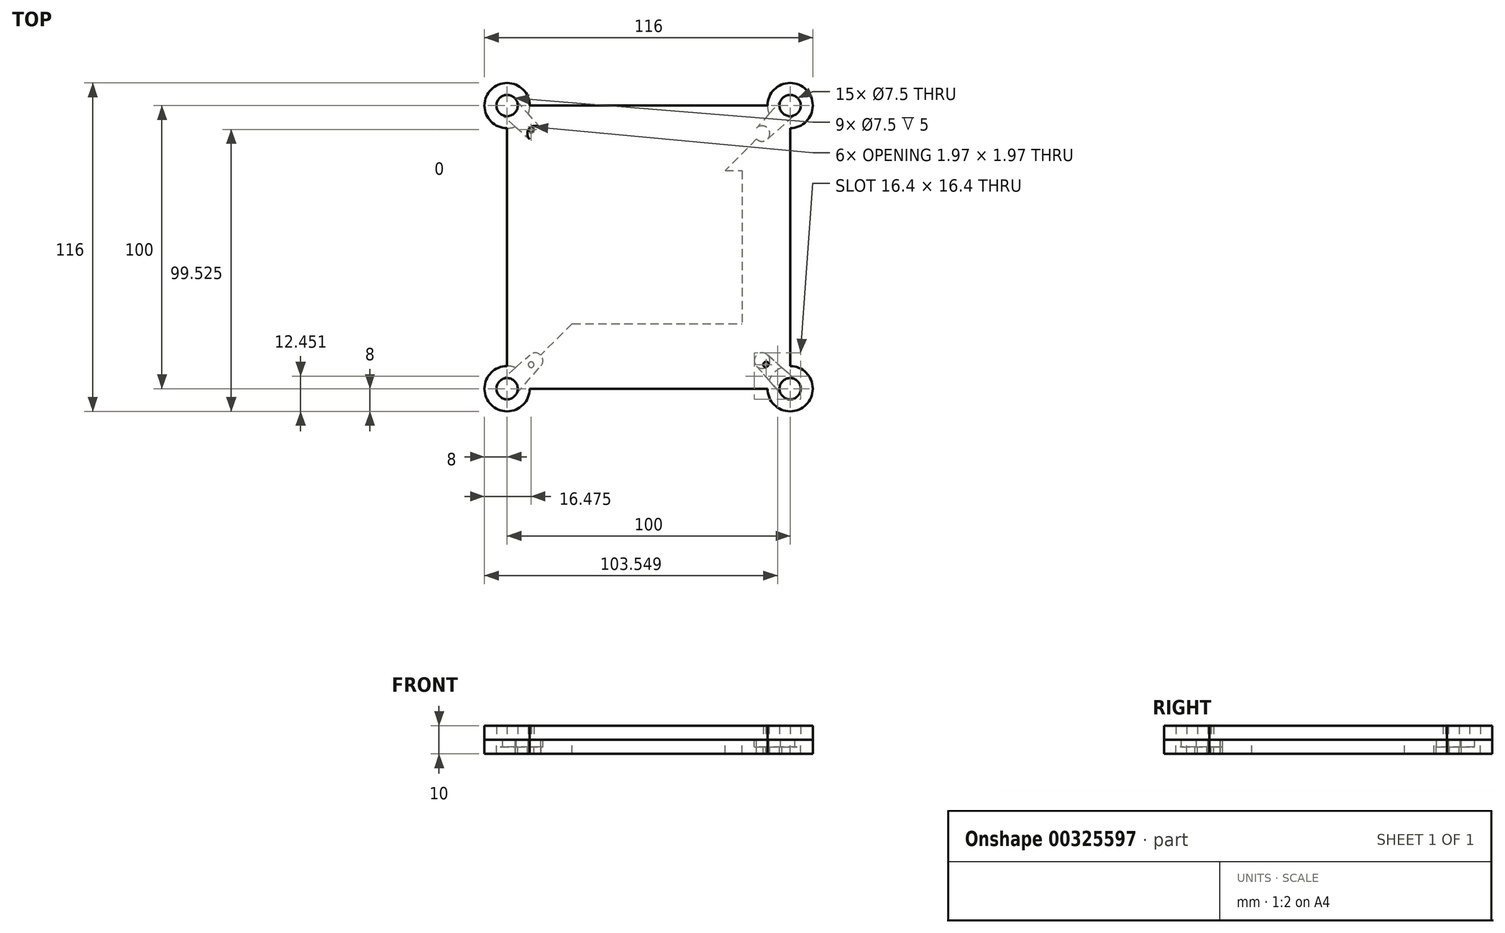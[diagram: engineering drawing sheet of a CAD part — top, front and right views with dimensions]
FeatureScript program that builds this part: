
annotation { "Feature Type Name" : "Feature", "Feature Type Description" : "" }
export const myFeature = defineFeature(function(context is Context, id is Id, definition is map)
    precondition{}
    {
        {
            var Q0;
            Q0=qCreatedBy(makeId("Top.planeOp"),FACE);
            var sketch = newSketch(context, id + "F0", { "sketchPlane" : qUnion([Q0])});
            skLineSegment(sketch, "E0.bottom", {"start": v(-50, 50) * mm, "end": v(50, 50) * mm});
            skLineSegment(sketch, "E0.top", {"start": v(-50, -50) * mm, "end": v(50, -50) * mm});
            skLineSegment(sketch, "E0.left", {"start": v(-50, 50) * mm, "end": v(-50, -50) * mm});
            skLineSegment(sketch, "E0.right", {"start": v(50, 50) * mm, "end": v(50, -50) * mm});
            skPoint(sketch, "E1", {"position": v(0, 50) * mm});
            skPoint(sketch, "E2", {"position": v(50, 0) * mm});
            skCircle(sketch, "E3", {"center": v(-50, 50) * mm, "radius": 1.5 * mm});
            skCircle(sketch, "E4", {"center": v(-50, -50) * mm, "radius": 1.5 * mm});
            skCircle(sketch, "E5", {"center": v(50, -50) * mm, "radius": 1.5 * mm});
            skCircle(sketch, "E6", {"center": v(50, 50) * mm, "radius": 1.5 * mm});
            skCircle(sketch, "E7", {"center": v(-50, 50) * mm, "radius": 8 * mm});
            skCircle(sketch, "E8", {"center": v(50, 50) * mm, "radius": 8 * mm});
            skCircle(sketch, "E9", {"center": v(50, -50) * mm, "radius": 8 * mm});
            skCircle(sketch, "E10", {"center": v(-50, -50) * mm, "radius": 8 * mm});
            skLineSegment(sketch, "E11.bottom", {"start": v(-33, 27) * mm, "end": v(33, 27) * mm});
            skLineSegment(sketch, "E11.top", {"start": v(-33, -27) * mm, "end": v(33, -27) * mm});
            skLineSegment(sketch, "E11.left", {"start": v(-33, 27) * mm, "end": v(-33, -27) * mm});
            skLineSegment(sketch, "E11.right", {"start": v(33, 27) * mm, "end": v(33, -27) * mm});
            skPoint(sketch, "E12", {"position": v(0, 27) * mm});
            skPoint(sketch, "E13", {"position": v(33, 0) * mm});
            skLineSegment(sketch, "E14", {"start": v(-50, 50) * mm, "end": v(50, -50) * mm});
            skLineSegment(sketch, "E15", {"start": v(50, 50) * mm, "end": v(-50, -50) * mm});
            skPoint(sketch, "E16", {"position": v(-41.51, 41.51) * mm});
            skPoint(sketch, "E17", {"position": v(40.1, 40.1) * mm});
            skPoint(sketch, "E18", {"position": v(40.1, -40.1) * mm});
            skPoint(sketch, "E19", {"position": v(-41.51, -41.51) * mm});
            skPoint(sketch, "E20", {"position": v(-40.1, -40.1) * mm});
            skPoint(sketch, "E21", {"position": v(-40.1, 40.1) * mm});
            skPoint(sketch, "E22", {"position": v(41.51, 41.51) * mm});
            skPoint(sketch, "E23", {"position": v(41.51, -41.51) * mm});
            skCircle(sketch, "E24", {"center": v(-50, 50) * mm, "radius": 3.75 * mm});
            skCircle(sketch, "E25", {"center": v(50, 50) * mm, "radius": 3.75 * mm});
            skCircle(sketch, "E26", {"center": v(-50, -50) * mm, "radius": 3.75 * mm});
            skCircle(sketch, "E27", {"center": v(50, -50) * mm, "radius": 3.75 * mm});
            skCircle(sketch, "E28", {"center": v(-41.51, 41.51) * mm, "radius": 1 * mm});
            skCircle(sketch, "E29", {"center": v(-40.1, 40.1) * mm, "radius": 2.75 * mm});
            skLineSegment(sketch, "E30", {"start": v(-46.7, 51.76) * mm, "end": v(-38.04, 41.92) * mm});
            skLineSegment(sketch, "E31", {"start": v(-42.02, 38.13) * mm, "end": v(-52.45, 47.16) * mm});
            skCircle(sketch, "E32", {"center": v(41.51, 41.51) * mm, "radius": 1 * mm});
            skCircle(sketch, "E33", {"center": v(40.1, 40.1) * mm, "radius": 2.75 * mm});
            skLineSegment(sketch, "E34", {"start": v(38.13, 42.02) * mm, "end": v(46.65, 51.68) * mm});
            skLineSegment(sketch, "E35", {"start": v(42.13, 38.24) * mm, "end": v(51.69, 46.65) * mm});
            skCircle(sketch, "E36", {"center": v(41.51, -41.51) * mm, "radius": 1 * mm});
            skCircle(sketch, "E37", {"center": v(40.1, -40.1) * mm, "radius": 2.75 * mm});
            skCircle(sketch, "E38", {"center": v(-41.51, -41.51) * mm, "radius": 1 * mm});
            skCircle(sketch, "E39", {"center": v(-40.1, -40.1) * mm, "radius": 2.75 * mm});
            skLineSegment(sketch, "E40", {"start": v(42, -38.11) * mm, "end": v(52.45, -47.17) * mm});
            skLineSegment(sketch, "E41", {"start": v(38.11, -42) * mm, "end": v(47.17, -52.45) * mm});
            skLineSegment(sketch, "E42", {"start": v(-41.93, -38.05) * mm, "end": v(-51.58, -46.6) * mm});
            skLineSegment(sketch, "E43", {"start": v(-46.76, -51.89) * mm, "end": v(-38.03, -41.91) * mm});
            skSolve(sketch);
        }
        {
            var Q0;
            {var subQ14=sQuery(id+"F0.wireOp",EDGE,"E11.left");Q0=makeQuery(id+"F0.imprint","IMPRINT",FACE,{"disambiguationData":[TD([[makeQuery(id+"F0.imprint","IMPRINT",EDGE,{"derivedFrom":subQ14}),-1.0]])]});}
            var Q1;
            {var subQ5=sQuery(id+"F0.wireOp",EDGE,"E11.left");Q1=makeQuery(id+"F0.imprint","IMPRINT",FACE,{"disambiguationData":[TD([[makeQuery(id+"F0.imprint","IMPRINT",EDGE,{"derivedFrom":subQ5}),1.0]])]});}
            var Q2;
            {var subQ0=sQuery(id+"F0.wireOp",EDGE,"E14");var subQ1=sQuery(id+"F0.wireOp",EDGE,"E11.bottom");var subQ2=makeQuery(id+"F0.imprint","INTERSECT",VERTEX,{"derivedFrom":[subQ1,subQ0]});Q2=makeQuery(id+"F0.imprint","IMPRINT",FACE,{"disambiguationData":[TD([[makeQuery(id+"F0.imprint","IMPRINT",EDGE,{"disambiguationData":[TD([[subQ2,-1.0]])],"derivedFrom":subQ1}),-1.0]])]});}
            var Q3;
            {var subQ0=sQuery(id+"F0.wireOp",EDGE,"E11.right");Q3=makeQuery(id+"F0.imprint","IMPRINT",FACE,{"disambiguationData":[TD([[makeQuery(id+"F0.imprint","IMPRINT",EDGE,{"derivedFrom":subQ0}),-1.0]])]});}
            var Q4;
            {var subQ0=sQuery(id+"F0.wireOp",EDGE,"E15");var subQ1=sQuery(id+"F0.wireOp",EDGE,"E11.top");var subQ2=makeQuery(id+"F0.imprint","INTERSECT",VERTEX,{"derivedFrom":[subQ1,subQ0]});Q4=makeQuery(id+"F0.imprint","IMPRINT",FACE,{"disambiguationData":[TD([[makeQuery(id+"F0.imprint","IMPRINT",EDGE,{"disambiguationData":[TD([[subQ2,-1.0]])],"derivedFrom":subQ1}),1.0]])]});}
            var Q5;
            {var subQ6=sQuery(id+"F0.wireOp",EDGE,"E0.top");var subQ10=sQuery(id+"F0.wireOp",EDGE,"E10");var subQ11=makeQuery(id+"F0.imprint","INTERSECT",VERTEX,{"derivedFrom":[subQ6,subQ10]});Q5=makeQuery(id+"F0.imprint","IMPRINT",FACE,{"disambiguationData":[TD([[makeQuery(id+"F0.imprint","IMPRINT",EDGE,{"disambiguationData":[TD([[subQ11,-1.0]])],"derivedFrom":subQ6}),1.0]])]});}
            var Q6;
            {var subQ0=sQuery(id+"F0.wireOp",EDGE,"E38");var subQ1=sQuery(id+"F0.wireOp",EDGE,"E15");var subQ2=makeQuery(id+"F0.imprint","INTERSECT",VERTEX,{"disambiguationData":[OD(0.0)],"derivedFrom":[subQ1,subQ0]});Q6=makeQuery(id+"F0.imprint","IMPRINT",FACE,{"disambiguationData":[TD([[makeQuery(id+"F0.imprint","IMPRINT",EDGE,{"disambiguationData":[TD([[subQ2,-1.0]])],"derivedFrom":subQ1}),1.0]])]});}
            var Q7;
            {var subQ5=sQuery(id+"F0.wireOp",EDGE,"E10");var subQ7=sQuery(id+"F0.wireOp",EDGE,"E15");var subQ8=makeQuery(id+"F0.imprint","INTERSECT",VERTEX,{"derivedFrom":[subQ5,subQ7]});Q7=makeQuery(id+"F0.imprint","IMPRINT",FACE,{"disambiguationData":[TD([[makeQuery(id+"F0.imprint","IMPRINT",EDGE,{"disambiguationData":[TD([[subQ8,-1.0]])],"derivedFrom":subQ5}),-1.0]])]});}
            var Q8;
            {var subQ0=sQuery(id+"F0.wireOp",EDGE,"E39");var subQ1=sQuery(id+"F0.wireOp",EDGE,"E15");var subQ2=makeQuery(id+"F0.imprint","INTERSECT",VERTEX,{"disambiguationData":[OD(1.0)],"derivedFrom":[subQ1,subQ0]});Q8=makeQuery(id+"F0.imprint","IMPRINT",FACE,{"disambiguationData":[TD([[makeQuery(id+"F0.imprint","IMPRINT",EDGE,{"disambiguationData":[TD([[subQ2,-1.0]])],"derivedFrom":subQ1}),-1.0]])]});}
            var Q9;
            {var subQ0=sQuery(id+"F0.wireOp",EDGE,"E39");var subQ1=sQuery(id+"F0.wireOp",EDGE,"E15");var subQ2=makeQuery(id+"F0.imprint","INTERSECT",VERTEX,{"disambiguationData":[OD(0.0)],"derivedFrom":[subQ1,subQ0]});Q9=makeQuery(id+"F0.imprint","IMPRINT",FACE,{"disambiguationData":[TD([[makeQuery(id+"F0.imprint","IMPRINT",EDGE,{"disambiguationData":[TD([[subQ2,-1.0]])],"derivedFrom":subQ1}),-1.0]])]});}
            var Q10;
            {var subQ0=sQuery(id+"F0.wireOp",EDGE,"E43");var subQ7=sQuery(id+"F0.wireOp",EDGE,"E10");var subQ9=makeQuery(id+"F0.imprint","INTERSECT",VERTEX,{"derivedFrom":[subQ7,subQ0]});Q10=makeQuery(id+"F0.imprint","IMPRINT",FACE,{"disambiguationData":[TD([[makeQuery(id+"F0.imprint","IMPRINT",EDGE,{"disambiguationData":[TD([[subQ9,-1.0]])],"derivedFrom":subQ7}),-1.0]])]});}
            var Q11;
            {var subQ0=sQuery(id+"F0.wireOp",EDGE,"E39");var subQ1=sQuery(id+"F0.wireOp",EDGE,"E15");var subQ2=makeQuery(id+"F0.imprint","INTERSECT",VERTEX,{"disambiguationData":[OD(0.0)],"derivedFrom":[subQ1,subQ0]});Q11=makeQuery(id+"F0.imprint","IMPRINT",FACE,{"disambiguationData":[TD([[makeQuery(id+"F0.imprint","IMPRINT",EDGE,{"disambiguationData":[TD([[subQ2,-1.0]])],"derivedFrom":subQ1}),1.0]])]});}
            var Q12;
            {var subQ0=sQuery(id+"F0.wireOp",EDGE,"E39");var subQ1=sQuery(id+"F0.wireOp",EDGE,"E15");var subQ2=makeQuery(id+"F0.imprint","INTERSECT",VERTEX,{"disambiguationData":[OD(1.0)],"derivedFrom":[subQ1,subQ0]});Q12=makeQuery(id+"F0.imprint","IMPRINT",FACE,{"disambiguationData":[TD([[makeQuery(id+"F0.imprint","IMPRINT",EDGE,{"disambiguationData":[TD([[subQ2,-1.0]])],"derivedFrom":subQ1}),1.0]])]});}
            var Q13;
            {var subQ0=sQuery(id+"F0.wireOp",EDGE,"E38");var subQ1=sQuery(id+"F0.wireOp",EDGE,"E15");var subQ2=makeQuery(id+"F0.imprint","INTERSECT",VERTEX,{"disambiguationData":[OD(0.0)],"derivedFrom":[subQ1,subQ0]});Q13=makeQuery(id+"F0.imprint","IMPRINT",FACE,{"disambiguationData":[TD([[makeQuery(id+"F0.imprint","IMPRINT",EDGE,{"disambiguationData":[TD([[subQ2,-1.0]])],"derivedFrom":subQ1}),-1.0]])]});}
            var Q14;
            {var subQ0=sQuery(id+"F0.wireOp",EDGE,"E40");var subQ6=sQuery(id+"F0.wireOp",EDGE,"E9");var subQ9=makeQuery(id+"F0.imprint","INTERSECT",VERTEX,{"derivedFrom":[subQ6,subQ0]});Q14=makeQuery(id+"F0.imprint","IMPRINT",FACE,{"disambiguationData":[TD([[makeQuery(id+"F0.imprint","IMPRINT",EDGE,{"disambiguationData":[TD([[subQ9,-1.0]])],"derivedFrom":subQ6}),-1.0]])]});}
            var Q15;
            {var subQ1=sQuery(id+"F0.wireOp",EDGE,"E14");var subQ7=sQuery(id+"F0.wireOp",EDGE,"E9");var subQ8=makeQuery(id+"F0.imprint","INTERSECT",VERTEX,{"derivedFrom":[subQ7,subQ1]});Q15=makeQuery(id+"F0.imprint","IMPRINT",FACE,{"disambiguationData":[TD([[makeQuery(id+"F0.imprint","IMPRINT",EDGE,{"disambiguationData":[TD([[subQ8,-1.0]])],"derivedFrom":subQ7}),-1.0]])]});}
            var Q16;
            {var subQ0=sQuery(id+"F0.wireOp",EDGE,"E37");var subQ1=sQuery(id+"F0.wireOp",EDGE,"E14");var subQ2=makeQuery(id+"F0.imprint","INTERSECT",VERTEX,{"disambiguationData":[OD(0.0)],"derivedFrom":[subQ1,subQ0]});Q16=makeQuery(id+"F0.imprint","IMPRINT",FACE,{"disambiguationData":[TD([[makeQuery(id+"F0.imprint","IMPRINT",EDGE,{"disambiguationData":[TD([[subQ2,-1.0]])],"derivedFrom":subQ1}),-1.0]])]});}
            var Q17;
            {var subQ0=sQuery(id+"F0.wireOp",EDGE,"E37");var subQ1=sQuery(id+"F0.wireOp",EDGE,"E14");var subQ2=makeQuery(id+"F0.imprint","INTERSECT",VERTEX,{"disambiguationData":[OD(0.0)],"derivedFrom":[subQ1,subQ0]});Q17=makeQuery(id+"F0.imprint","IMPRINT",FACE,{"disambiguationData":[TD([[makeQuery(id+"F0.imprint","IMPRINT",EDGE,{"disambiguationData":[TD([[subQ2,-1.0]])],"derivedFrom":subQ1}),1.0]])]});}
            var Q18;
            {var subQ0=sQuery(id+"F0.wireOp",EDGE,"E37");var subQ1=sQuery(id+"F0.wireOp",EDGE,"E14");var subQ2=makeQuery(id+"F0.imprint","INTERSECT",VERTEX,{"disambiguationData":[OD(1.0)],"derivedFrom":[subQ1,subQ0]});Q18=makeQuery(id+"F0.imprint","IMPRINT",FACE,{"disambiguationData":[TD([[makeQuery(id+"F0.imprint","IMPRINT",EDGE,{"disambiguationData":[TD([[subQ2,-1.0]])],"derivedFrom":subQ1}),1.0]])]});}
            var Q19;
            {var subQ0=sQuery(id+"F0.wireOp",EDGE,"E36");var subQ1=sQuery(id+"F0.wireOp",EDGE,"E14");var subQ2=makeQuery(id+"F0.imprint","INTERSECT",VERTEX,{"disambiguationData":[OD(0.0)],"derivedFrom":[subQ1,subQ0]});Q19=makeQuery(id+"F0.imprint","IMPRINT",FACE,{"disambiguationData":[TD([[makeQuery(id+"F0.imprint","IMPRINT",EDGE,{"disambiguationData":[TD([[subQ2,-1.0]])],"derivedFrom":subQ1}),1.0]])]});}
            var Q20;
            {var subQ0=sQuery(id+"F0.wireOp",EDGE,"E36");var subQ1=sQuery(id+"F0.wireOp",EDGE,"E14");var subQ2=makeQuery(id+"F0.imprint","INTERSECT",VERTEX,{"disambiguationData":[OD(0.0)],"derivedFrom":[subQ1,subQ0]});Q20=makeQuery(id+"F0.imprint","IMPRINT",FACE,{"disambiguationData":[TD([[makeQuery(id+"F0.imprint","IMPRINT",EDGE,{"disambiguationData":[TD([[subQ2,-1.0]])],"derivedFrom":subQ1}),-1.0]])]});}
            var Q21;
            {var subQ0=sQuery(id+"F0.wireOp",EDGE,"E37");var subQ1=sQuery(id+"F0.wireOp",EDGE,"E14");var subQ2=makeQuery(id+"F0.imprint","INTERSECT",VERTEX,{"disambiguationData":[OD(1.0)],"derivedFrom":[subQ1,subQ0]});Q21=makeQuery(id+"F0.imprint","IMPRINT",FACE,{"disambiguationData":[TD([[makeQuery(id+"F0.imprint","IMPRINT",EDGE,{"disambiguationData":[TD([[subQ2,-1.0]])],"derivedFrom":subQ1}),-1.0]])]});}
            var Q22;
            {var subQ0=sQuery(id+"F0.wireOp",EDGE,"E32");var subQ1=sQuery(id+"F0.wireOp",EDGE,"E15");var subQ2=makeQuery(id+"F0.imprint","INTERSECT",VERTEX,{"disambiguationData":[OD(1.0)],"derivedFrom":[subQ1,subQ0]});Q22=makeQuery(id+"F0.imprint","IMPRINT",FACE,{"disambiguationData":[TD([[makeQuery(id+"F0.imprint","IMPRINT",EDGE,{"disambiguationData":[TD([[subQ2,-1.0]])],"derivedFrom":subQ1}),1.0]])]});}
            var Q23;
            {var subQ0=sQuery(id+"F0.wireOp",EDGE,"E33");var subQ1=sQuery(id+"F0.wireOp",EDGE,"E15");var subQ2=makeQuery(id+"F0.imprint","INTERSECT",VERTEX,{"disambiguationData":[OD(0.0)],"derivedFrom":[subQ1,subQ0]});Q23=makeQuery(id+"F0.imprint","IMPRINT",FACE,{"disambiguationData":[TD([[makeQuery(id+"F0.imprint","IMPRINT",EDGE,{"disambiguationData":[TD([[subQ2,-1.0]])],"derivedFrom":subQ1}),1.0]])]});}
            var Q24;
            {var subQ0=sQuery(id+"F0.wireOp",EDGE,"E32");var subQ1=sQuery(id+"F0.wireOp",EDGE,"E15");var subQ2=makeQuery(id+"F0.imprint","INTERSECT",VERTEX,{"disambiguationData":[OD(0.0)],"derivedFrom":[subQ1,subQ0]});Q24=makeQuery(id+"F0.imprint","IMPRINT",FACE,{"disambiguationData":[TD([[makeQuery(id+"F0.imprint","IMPRINT",EDGE,{"disambiguationData":[TD([[subQ2,-1.0]])],"derivedFrom":subQ1}),1.0]])]});}
            var Q25;
            {var subQ0=sQuery(id+"F0.wireOp",EDGE,"E34");var subQ7=sQuery(id+"F0.wireOp",EDGE,"E8");var subQ9=makeQuery(id+"F0.imprint","INTERSECT",VERTEX,{"derivedFrom":[subQ7,subQ0]});Q25=makeQuery(id+"F0.imprint","IMPRINT",FACE,{"disambiguationData":[TD([[makeQuery(id+"F0.imprint","IMPRINT",EDGE,{"disambiguationData":[TD([[subQ9,-1.0]])],"derivedFrom":subQ7}),-1.0]])]});}
            var Q26;
            {var subQ0=sQuery(id+"F0.wireOp",EDGE,"E32");var subQ1=sQuery(id+"F0.wireOp",EDGE,"E15");var subQ2=makeQuery(id+"F0.imprint","INTERSECT",VERTEX,{"disambiguationData":[OD(0.0)],"derivedFrom":[subQ1,subQ0]});Q26=makeQuery(id+"F0.imprint","IMPRINT",FACE,{"disambiguationData":[TD([[makeQuery(id+"F0.imprint","IMPRINT",EDGE,{"disambiguationData":[TD([[subQ2,-1.0]])],"derivedFrom":subQ1}),-1.0]])]});}
            var Q27;
            {var subQ0=sQuery(id+"F0.wireOp",EDGE,"E33");var subQ1=sQuery(id+"F0.wireOp",EDGE,"E15");var subQ2=makeQuery(id+"F0.imprint","INTERSECT",VERTEX,{"disambiguationData":[OD(0.0)],"derivedFrom":[subQ1,subQ0]});Q27=makeQuery(id+"F0.imprint","IMPRINT",FACE,{"disambiguationData":[TD([[makeQuery(id+"F0.imprint","IMPRINT",EDGE,{"disambiguationData":[TD([[subQ2,-1.0]])],"derivedFrom":subQ1}),-1.0]])]});}
            var Q28;
            {var subQ5=sQuery(id+"F0.wireOp",EDGE,"E15");var subQ6=sQuery(id+"F0.wireOp",EDGE,"E8");var subQ7=makeQuery(id+"F0.imprint","INTERSECT",VERTEX,{"derivedFrom":[subQ6,subQ5]});Q28=makeQuery(id+"F0.imprint","IMPRINT",FACE,{"disambiguationData":[TD([[makeQuery(id+"F0.imprint","IMPRINT",EDGE,{"disambiguationData":[TD([[subQ7,-1.0]])],"derivedFrom":subQ6}),-1.0]])]});}
            var Q29;
            {var subQ0=sQuery(id+"F0.wireOp",EDGE,"E32");var subQ1=sQuery(id+"F0.wireOp",EDGE,"E15");var subQ2=makeQuery(id+"F0.imprint","INTERSECT",VERTEX,{"disambiguationData":[OD(1.0)],"derivedFrom":[subQ1,subQ0]});Q29=makeQuery(id+"F0.imprint","IMPRINT",FACE,{"disambiguationData":[TD([[makeQuery(id+"F0.imprint","IMPRINT",EDGE,{"disambiguationData":[TD([[subQ2,-1.0]])],"derivedFrom":subQ1}),-1.0]])]});}
            var Q30;
            {var subQ1=sQuery(id+"F0.wireOp",EDGE,"E0.bottom");var subQ5=sQuery(id+"F0.wireOp",EDGE,"E7");var subQ6=makeQuery(id+"F0.imprint","INTERSECT",VERTEX,{"derivedFrom":[subQ1,subQ5]});Q30=makeQuery(id+"F0.imprint","IMPRINT",FACE,{"disambiguationData":[TD([[makeQuery(id+"F0.imprint","IMPRINT",EDGE,{"disambiguationData":[TD([[subQ6,-1.0]])],"derivedFrom":subQ1}),-1.0]])]});}
            var Q31;
            {var subQ0=sQuery(id+"F0.wireOp",EDGE,"E7");var subQ1=sQuery(id+"F0.wireOp",EDGE,"E0.bottom");var subQ2=makeQuery(id+"F0.imprint","INTERSECT",VERTEX,{"derivedFrom":[subQ1,subQ0]});Q31=makeQuery(id+"F0.imprint","IMPRINT",FACE,{"disambiguationData":[TD([[makeQuery(id+"F0.imprint","IMPRINT",EDGE,{"disambiguationData":[TD([[subQ2,1.0]])],"derivedFrom":subQ1}),-1.0]])]});}
            var Q32;
            {var subQ0=sQuery(id+"F0.wireOp",EDGE,"E29");var subQ1=sQuery(id+"F0.wireOp",EDGE,"E14");var subQ2=makeQuery(id+"F0.imprint","INTERSECT",VERTEX,{"disambiguationData":[OD(0.0)],"derivedFrom":[subQ1,subQ0]});Q32=makeQuery(id+"F0.imprint","IMPRINT",FACE,{"disambiguationData":[TD([[makeQuery(id+"F0.imprint","IMPRINT",EDGE,{"disambiguationData":[TD([[subQ2,-1.0]])],"derivedFrom":subQ1}),-1.0]])]});}
            var Q33;
            {var subQ0=sQuery(id+"F0.wireOp",EDGE,"E28");var subQ1=sQuery(id+"F0.wireOp",EDGE,"E14");var subQ2=makeQuery(id+"F0.imprint","INTERSECT",VERTEX,{"disambiguationData":[OD(1.0)],"derivedFrom":[subQ1,subQ0]});Q33=makeQuery(id+"F0.imprint","IMPRINT",FACE,{"disambiguationData":[TD([[makeQuery(id+"F0.imprint","IMPRINT",EDGE,{"disambiguationData":[TD([[subQ2,-1.0]])],"derivedFrom":subQ1}),1.0]])]});}
            var Q34;
            {var subQ0=sQuery(id+"F0.wireOp",EDGE,"E29");var subQ1=sQuery(id+"F0.wireOp",EDGE,"E14");var subQ2=makeQuery(id+"F0.imprint","INTERSECT",VERTEX,{"disambiguationData":[OD(0.0)],"derivedFrom":[subQ1,subQ0]});Q34=makeQuery(id+"F0.imprint","IMPRINT",FACE,{"disambiguationData":[TD([[makeQuery(id+"F0.imprint","IMPRINT",EDGE,{"disambiguationData":[TD([[subQ2,-1.0]])],"derivedFrom":subQ1}),1.0]])]});}
            var Q35;
            {var subQ0=sQuery(id+"F0.wireOp",EDGE,"E7");var subQ1=sQuery(id+"F0.wireOp",EDGE,"E0.left");var subQ2=makeQuery(id+"F0.imprint","INTERSECT",VERTEX,{"derivedFrom":[subQ1,subQ0]});Q35=makeQuery(id+"F0.imprint","IMPRINT",FACE,{"disambiguationData":[TD([[makeQuery(id+"F0.imprint","IMPRINT",EDGE,{"disambiguationData":[TD([[subQ2,1.0]])],"derivedFrom":subQ1}),1.0]])]});}
            var Q36;
            {var subQ0=sQuery(id+"F0.wireOp",EDGE,"E31");var subQ7=sQuery(id+"F0.wireOp",EDGE,"E7");var subQ9=makeQuery(id+"F0.imprint","INTERSECT",VERTEX,{"derivedFrom":[subQ7,subQ0]});Q36=makeQuery(id+"F0.imprint","IMPRINT",FACE,{"disambiguationData":[TD([[makeQuery(id+"F0.imprint","IMPRINT",EDGE,{"disambiguationData":[TD([[subQ9,-1.0]])],"derivedFrom":subQ7}),-1.0]])]});}
            var Q37;
            {var subQ0=sQuery(id+"F0.wireOp",EDGE,"E28");var subQ1=sQuery(id+"F0.wireOp",EDGE,"E14");var subQ2=makeQuery(id+"F0.imprint","INTERSECT",VERTEX,{"disambiguationData":[OD(1.0)],"derivedFrom":[subQ1,subQ0]});Q37=makeQuery(id+"F0.imprint","IMPRINT",FACE,{"disambiguationData":[TD([[makeQuery(id+"F0.imprint","IMPRINT",EDGE,{"disambiguationData":[TD([[subQ2,-1.0]])],"derivedFrom":subQ1}),-1.0]])]});}
            var Q38;
            {var subQ0=sQuery(id+"F0.wireOp",EDGE,"E28");var subQ1=sQuery(id+"F0.wireOp",EDGE,"E14");var subQ2=makeQuery(id+"F0.imprint","INTERSECT",VERTEX,{"disambiguationData":[OD(0.0)],"derivedFrom":[subQ1,subQ0]});Q38=makeQuery(id+"F0.imprint","IMPRINT",FACE,{"disambiguationData":[TD([[makeQuery(id+"F0.imprint","IMPRINT",EDGE,{"disambiguationData":[TD([[subQ2,-1.0]])],"derivedFrom":subQ1}),-1.0]])]});}
            var Q39;
            {var subQ1=sQuery(id+"F0.wireOp",EDGE,"E14");var subQ7=sQuery(id+"F0.wireOp",EDGE,"E7");var subQ8=makeQuery(id+"F0.imprint","INTERSECT",VERTEX,{"derivedFrom":[subQ7,subQ1]});Q39=makeQuery(id+"F0.imprint","IMPRINT",FACE,{"disambiguationData":[TD([[makeQuery(id+"F0.imprint","IMPRINT",EDGE,{"disambiguationData":[TD([[subQ8,-1.0]])],"derivedFrom":subQ7}),-1.0]])]});}
            var Q40;
            {var subQ0=sQuery(id+"F0.wireOp",EDGE,"E24");var subQ1=sQuery(id+"F0.wireOp",EDGE,"E0.left");var subQ2=makeQuery(id+"F0.imprint","INTERSECT",VERTEX,{"derivedFrom":[subQ1,subQ0]});Q40=makeQuery(id+"F0.imprint","IMPRINT",FACE,{"disambiguationData":[TD([[makeQuery(id+"F0.imprint","IMPRINT",EDGE,{"disambiguationData":[TD([[subQ2,-1.0]])],"derivedFrom":subQ1}),1.0]])]});}
            var Q41;
            {var subQ0=sQuery(id+"F0.wireOp",EDGE,"E28");var subQ1=sQuery(id+"F0.wireOp",EDGE,"E14");var subQ2=makeQuery(id+"F0.imprint","INTERSECT",VERTEX,{"disambiguationData":[OD(0.0)],"derivedFrom":[subQ1,subQ0]});Q41=makeQuery(id+"F0.imprint","IMPRINT",FACE,{"disambiguationData":[TD([[makeQuery(id+"F0.imprint","IMPRINT",EDGE,{"disambiguationData":[TD([[subQ2,-1.0]])],"derivedFrom":subQ1}),1.0]])]});}
            var Q42;
            {var subQ3=sQuery(id+"F0.wireOp",EDGE,"E24");var subQ7=sQuery(id+"F0.wireOp",EDGE,"E0.bottom");var subQ8=makeQuery(id+"F0.imprint","INTERSECT",VERTEX,{"derivedFrom":[subQ7,subQ3]});Q42=makeQuery(id+"F0.imprint","IMPRINT",FACE,{"disambiguationData":[TD([[makeQuery(id+"F0.imprint","IMPRINT",EDGE,{"disambiguationData":[TD([[subQ8,-1.0]])],"derivedFrom":subQ7}),-1.0]])]});}
            var Q43;
            {var subQ5=sQuery(id+"F0.wireOp",EDGE,"E11.right");Q43=makeQuery(id+"F0.imprint","IMPRINT",FACE,{"disambiguationData":[TD([[makeQuery(id+"F0.imprint","IMPRINT",EDGE,{"derivedFrom":subQ5}),1.0]])]});}
            var Q44;
            {var subQ0=sQuery(id+"F0.wireOp",EDGE,"E10");var subQ5=sQuery(id+"F0.wireOp",EDGE,"E0.top");var subQ6=makeQuery(id+"F0.imprint","INTERSECT",VERTEX,{"derivedFrom":[subQ5,subQ0]});Q44=makeQuery(id+"F0.imprint","IMPRINT",FACE,{"disambiguationData":[TD([[makeQuery(id+"F0.imprint","IMPRINT",EDGE,{"disambiguationData":[TD([[subQ6,1.0]])],"derivedFrom":subQ5}),-1.0]])]});}
            var Q45;
            {var subQ1=sQuery(id+"F0.wireOp",EDGE,"E0.left");var subQ7=sQuery(id+"F0.wireOp",EDGE,"E42");var subQ9=makeQuery(id+"F0.imprint","INTERSECT",VERTEX,{"derivedFrom":[subQ1,subQ7]});Q45=makeQuery(id+"F0.imprint","IMPRINT",FACE,{"disambiguationData":[TD([[makeQuery(id+"F0.imprint","IMPRINT",EDGE,{"disambiguationData":[TD([[subQ9,-1.0]])],"derivedFrom":subQ1}),1.0]])]});}
            var Q46;
            {var subQ0=sQuery(id+"F0.wireOp",EDGE,"E10");var subQ1=sQuery(id+"F0.wireOp",EDGE,"E0.left");var subQ2=makeQuery(id+"F0.imprint","INTERSECT",VERTEX,{"derivedFrom":[subQ1,subQ0]});Q46=makeQuery(id+"F0.imprint","IMPRINT",FACE,{"disambiguationData":[TD([[makeQuery(id+"F0.imprint","IMPRINT",EDGE,{"disambiguationData":[TD([[subQ2,-1.0]])],"derivedFrom":subQ1}),1.0]])]});}
            var Q47;
            {var subQ0=sQuery(id+"F0.wireOp",EDGE,"E26");var subQ1=sQuery(id+"F0.wireOp",EDGE,"E0.top");var subQ2=makeQuery(id+"F0.imprint","INTERSECT",VERTEX,{"derivedFrom":[subQ1,subQ0]});Q47=makeQuery(id+"F0.imprint","IMPRINT",FACE,{"disambiguationData":[TD([[makeQuery(id+"F0.imprint","IMPRINT",EDGE,{"disambiguationData":[TD([[subQ2,-1.0]])],"derivedFrom":subQ1}),1.0]])]});}
            var Q48;
            {var subQ0=sQuery(id+"F0.wireOp",EDGE,"E10");var subQ1=sQuery(id+"F0.wireOp",EDGE,"E0.top");var subQ2=makeQuery(id+"F0.imprint","INTERSECT",VERTEX,{"derivedFrom":[subQ1,subQ0]});Q48=makeQuery(id+"F0.imprint","IMPRINT",FACE,{"disambiguationData":[TD([[makeQuery(id+"F0.imprint","IMPRINT",EDGE,{"disambiguationData":[TD([[subQ2,1.0]])],"derivedFrom":subQ1}),1.0]])]});}
            var Q49;
            {var subQ0=sQuery(id+"F0.wireOp",EDGE,"E26");var subQ1=sQuery(id+"F0.wireOp",EDGE,"E0.top");var subQ2=makeQuery(id+"F0.imprint","INTERSECT",VERTEX,{"derivedFrom":[subQ1,subQ0]});Q49=makeQuery(id+"F0.imprint","IMPRINT",FACE,{"disambiguationData":[TD([[makeQuery(id+"F0.imprint","IMPRINT",EDGE,{"disambiguationData":[TD([[subQ2,-1.0]])],"derivedFrom":subQ1}),-1.0]])]});}
            var Q50;
            {var subQ0=sQuery(id+"F0.wireOp",EDGE,"E42");var subQ1=sQuery(id+"F0.wireOp",EDGE,"E0.left");var subQ2=makeQuery(id+"F0.imprint","INTERSECT",VERTEX,{"derivedFrom":[subQ1,subQ0]});Q50=makeQuery(id+"F0.imprint","IMPRINT",FACE,{"disambiguationData":[TD([[makeQuery(id+"F0.imprint","IMPRINT",EDGE,{"disambiguationData":[TD([[subQ2,-1.0]])],"derivedFrom":subQ1}),-1.0]])]});}
            var Q51;
            {var subQ0=sQuery(id+"F0.wireOp",EDGE,"E9");var subQ1=sQuery(id+"F0.wireOp",EDGE,"E0.top");var subQ2=makeQuery(id+"F0.imprint","INTERSECT",VERTEX,{"derivedFrom":[subQ1,subQ0]});Q51=makeQuery(id+"F0.imprint","IMPRINT",FACE,{"disambiguationData":[TD([[makeQuery(id+"F0.imprint","IMPRINT",EDGE,{"disambiguationData":[TD([[subQ2,-1.0]])],"derivedFrom":subQ1}),1.0]])]});}
            var Q52;
            {var subQ1=sQuery(id+"F0.wireOp",EDGE,"E0.top");var subQ7=sQuery(id+"F0.wireOp",EDGE,"E41");var subQ9=makeQuery(id+"F0.imprint","INTERSECT",VERTEX,{"derivedFrom":[subQ1,subQ7]});Q52=makeQuery(id+"F0.imprint","IMPRINT",FACE,{"disambiguationData":[TD([[makeQuery(id+"F0.imprint","IMPRINT",EDGE,{"disambiguationData":[TD([[subQ9,-1.0]])],"derivedFrom":subQ1}),1.0]])]});}
            var Q53;
            {var subQ1=sQuery(id+"F0.wireOp",EDGE,"E0.right");var subQ7=sQuery(id+"F0.wireOp",EDGE,"E40");var subQ8=makeQuery(id+"F0.imprint","INTERSECT",VERTEX,{"derivedFrom":[subQ1,subQ7]});Q53=makeQuery(id+"F0.imprint","IMPRINT",FACE,{"disambiguationData":[TD([[makeQuery(id+"F0.imprint","IMPRINT",EDGE,{"disambiguationData":[TD([[subQ8,-1.0]])],"derivedFrom":subQ1}),-1.0]])]});}
            var Q54;
            {var subQ0=sQuery(id+"F0.wireOp",EDGE,"E9");var subQ1=sQuery(id+"F0.wireOp",EDGE,"E0.right");var subQ2=makeQuery(id+"F0.imprint","INTERSECT",VERTEX,{"derivedFrom":[subQ1,subQ0]});Q54=makeQuery(id+"F0.imprint","IMPRINT",FACE,{"disambiguationData":[TD([[makeQuery(id+"F0.imprint","IMPRINT",EDGE,{"disambiguationData":[TD([[subQ2,-1.0]])],"derivedFrom":subQ1}),-1.0]])]});}
            var Q55;
            {var subQ0=sQuery(id+"F0.wireOp",EDGE,"E9");var subQ1=sQuery(id+"F0.wireOp",EDGE,"E0.top");var subQ2=makeQuery(id+"F0.imprint","INTERSECT",VERTEX,{"derivedFrom":[subQ1,subQ0]});Q55=makeQuery(id+"F0.imprint","IMPRINT",FACE,{"disambiguationData":[TD([[makeQuery(id+"F0.imprint","IMPRINT",EDGE,{"disambiguationData":[TD([[subQ2,-1.0]])],"derivedFrom":subQ1}),-1.0]])]});}
            var Q56;
            {var subQ0=sQuery(id+"F0.wireOp",EDGE,"E41");var subQ1=sQuery(id+"F0.wireOp",EDGE,"E0.top");var subQ2=makeQuery(id+"F0.imprint","INTERSECT",VERTEX,{"derivedFrom":[subQ1,subQ0]});Q56=makeQuery(id+"F0.imprint","IMPRINT",FACE,{"disambiguationData":[TD([[makeQuery(id+"F0.imprint","IMPRINT",EDGE,{"disambiguationData":[TD([[subQ2,-1.0]])],"derivedFrom":subQ1}),-1.0]])]});}
            var Q57;
            {var subQ0=sQuery(id+"F0.wireOp",EDGE,"E40");var subQ1=sQuery(id+"F0.wireOp",EDGE,"E0.right");var subQ2=makeQuery(id+"F0.imprint","INTERSECT",VERTEX,{"derivedFrom":[subQ1,subQ0]});Q57=makeQuery(id+"F0.imprint","IMPRINT",FACE,{"disambiguationData":[TD([[makeQuery(id+"F0.imprint","IMPRINT",EDGE,{"disambiguationData":[TD([[subQ2,-1.0]])],"derivedFrom":subQ1}),1.0]])]});}
            var Q58;
            {var subQ4=sQuery(id+"F0.wireOp",EDGE,"E8");var subQ5=sQuery(id+"F0.wireOp",EDGE,"E0.bottom");var subQ6=makeQuery(id+"F0.imprint","INTERSECT",VERTEX,{"derivedFrom":[subQ5,subQ4]});Q58=makeQuery(id+"F0.imprint","IMPRINT",FACE,{"disambiguationData":[TD([[makeQuery(id+"F0.imprint","IMPRINT",EDGE,{"disambiguationData":[TD([[subQ6,-1.0]])],"derivedFrom":subQ5}),1.0]])]});}
            var Q59;
            {var subQ0=sQuery(id+"F0.wireOp",EDGE,"E8");var subQ1=sQuery(id+"F0.wireOp",EDGE,"E0.bottom");var subQ2=makeQuery(id+"F0.imprint","INTERSECT",VERTEX,{"derivedFrom":[subQ1,subQ0]});Q59=makeQuery(id+"F0.imprint","IMPRINT",FACE,{"disambiguationData":[TD([[makeQuery(id+"F0.imprint","IMPRINT",EDGE,{"disambiguationData":[TD([[subQ2,-1.0]])],"derivedFrom":subQ1}),-1.0]])]});}
            var Q60;
            {var subQ1=sQuery(id+"F0.wireOp",EDGE,"E0.bottom");var subQ5=sQuery(id+"F0.wireOp",EDGE,"E34");var subQ6=makeQuery(id+"F0.imprint","INTERSECT",VERTEX,{"derivedFrom":[subQ1,subQ5]});Q60=makeQuery(id+"F0.imprint","IMPRINT",FACE,{"disambiguationData":[TD([[makeQuery(id+"F0.imprint","IMPRINT",EDGE,{"disambiguationData":[TD([[subQ6,-1.0]])],"derivedFrom":subQ1}),-1.0]])]});}
            var Q61;
            {var subQ3=sQuery(id+"F0.wireOp",EDGE,"E25");var subQ5=sQuery(id+"F0.wireOp",EDGE,"E0.right");var subQ6=makeQuery(id+"F0.imprint","INTERSECT",VERTEX,{"derivedFrom":[subQ5,subQ3]});Q61=makeQuery(id+"F0.imprint","IMPRINT",FACE,{"disambiguationData":[TD([[makeQuery(id+"F0.imprint","IMPRINT",EDGE,{"disambiguationData":[TD([[subQ6,-1.0]])],"derivedFrom":subQ5}),-1.0]])]});}
            var Q62;
            {var subQ0=sQuery(id+"F0.wireOp",EDGE,"E25");var subQ1=sQuery(id+"F0.wireOp",EDGE,"E0.right");var subQ2=makeQuery(id+"F0.imprint","INTERSECT",VERTEX,{"derivedFrom":[subQ1,subQ0]});Q62=makeQuery(id+"F0.imprint","IMPRINT",FACE,{"disambiguationData":[TD([[makeQuery(id+"F0.imprint","IMPRINT",EDGE,{"disambiguationData":[TD([[subQ2,-1.0]])],"derivedFrom":subQ1}),1.0]])]});}
            var Q63;
            {var subQ0=sQuery(id+"F0.wireOp",EDGE,"E8");var subQ1=sQuery(id+"F0.wireOp",EDGE,"E0.right");var subQ2=makeQuery(id+"F0.imprint","INTERSECT",VERTEX,{"derivedFrom":[subQ1,subQ0]});Q63=makeQuery(id+"F0.imprint","IMPRINT",FACE,{"disambiguationData":[TD([[makeQuery(id+"F0.imprint","IMPRINT",EDGE,{"disambiguationData":[TD([[subQ2,1.0]])],"derivedFrom":subQ1}),-1.0]])]});}
            var Q64;
            {var subQ0=sQuery(id+"F0.wireOp",EDGE,"E34");var subQ1=sQuery(id+"F0.wireOp",EDGE,"E0.bottom");var subQ2=makeQuery(id+"F0.imprint","INTERSECT",VERTEX,{"derivedFrom":[subQ1,subQ0]});Q64=makeQuery(id+"F0.imprint","IMPRINT",FACE,{"disambiguationData":[TD([[makeQuery(id+"F0.imprint","IMPRINT",EDGE,{"disambiguationData":[TD([[subQ2,-1.0]])],"derivedFrom":subQ1}),1.0]])]});}
            var Q65;
            {var subQ0=sQuery(id+"F0.wireOp",EDGE,"E7");var subQ9=sQuery(id+"F0.wireOp",EDGE,"E0.bottom");var subQ10=makeQuery(id+"F0.imprint","INTERSECT",VERTEX,{"derivedFrom":[subQ9,subQ0]});Q65=makeQuery(id+"F0.imprint","IMPRINT",FACE,{"disambiguationData":[TD([[makeQuery(id+"F0.imprint","IMPRINT",EDGE,{"disambiguationData":[TD([[subQ10,1.0]])],"derivedFrom":subQ9}),1.0]])]});}
            var Q66;
            {var subQ0=sQuery(id+"F0.wireOp",EDGE,"E24");var subQ1=sQuery(id+"F0.wireOp",EDGE,"E0.left");var subQ2=makeQuery(id+"F0.imprint","INTERSECT",VERTEX,{"derivedFrom":[subQ1,subQ0]});Q66=makeQuery(id+"F0.imprint","IMPRINT",FACE,{"disambiguationData":[TD([[makeQuery(id+"F0.imprint","IMPRINT",EDGE,{"disambiguationData":[TD([[subQ2,-1.0]])],"derivedFrom":subQ1}),-1.0]])]});}
            var Q67;
            {var subQ0=sQuery(id+"F0.wireOp",EDGE,"E24");var subQ1=sQuery(id+"F0.wireOp",EDGE,"E0.bottom");var subQ2=makeQuery(id+"F0.imprint","INTERSECT",VERTEX,{"derivedFrom":[subQ1,subQ0]});Q67=makeQuery(id+"F0.imprint","IMPRINT",FACE,{"disambiguationData":[TD([[makeQuery(id+"F0.imprint","IMPRINT",EDGE,{"disambiguationData":[TD([[subQ2,-1.0]])],"derivedFrom":subQ1}),1.0]])]});}
            extrude(context, id + "F1", {"entities" : qUnion([Q0, Q1, Q2, Q3, Q4, Q5, Q6, Q7, Q8, Q9, Q10, Q11, Q12, Q13, Q14, Q15, Q16, Q17, Q18, Q19, Q20, Q21, Q22, Q23, Q24, Q25, Q26, Q27, Q28, Q29, Q30, Q31, Q32, Q33, Q34, Q35, Q36, Q37, Q38, Q39, Q40, Q41, Q42, Q43, Q44, Q45, Q46, Q47, Q48, Q49, Q50, Q51, Q52, Q53, Q54, Q55, Q56, Q57, Q58, Q59, Q60, Q61, Q62, Q63, Q64, Q65, Q66, Q67]), "depth" : 5 * mm});
        }
        {
            var Q0;
            Q0=makeQuery(id+"F1.opExtrude","SWEPT_BODY",BODY,{"disambiguationData":[OSD([sQuery(id+"F0.wireOp",EDGE,"E0.bottom"),sQuery(id+"F0.wireOp",EDGE,"E0.top"),sQuery(id+"F0.wireOp",EDGE,"E0.left"),sQuery(id+"F0.wireOp",EDGE,"E0.right"),sQuery(id+"F0.wireOp",EDGE,"E3"),sQuery(id+"F0.wireOp",EDGE,"E4"),sQuery(id+"F0.wireOp",EDGE,"E5"),sQuery(id+"F0.wireOp",EDGE,"E6"),sQuery(id+"F0.wireOp",EDGE,"E7"),sQuery(id+"F0.wireOp",EDGE,"E8"),sQuery(id+"F0.wireOp",EDGE,"E9"),sQuery(id+"F0.wireOp",EDGE,"E10"),sQuery(id+"F0.wireOp",EDGE,"E24"),sQuery(id+"F0.wireOp",EDGE,"E25"),sQuery(id+"F0.wireOp",EDGE,"E26"),sQuery(id+"F0.wireOp",EDGE,"E30"),sQuery(id+"F0.wireOp",EDGE,"E35"),sQuery(id+"F0.wireOp",EDGE,"E43")])]});
            var Q1;
            Q1=qCreatedBy(makeId("Top.planeOp"),FACE);
            mirror(context, id + "F2", {"entities" : qUnion([Q0]), "mirrorPlane" : qUnion([Q1])});
        }
        {
            var Q0;
            {var subQ5=sQuery(id+"F0.wireOp",EDGE,"E11.left");Q0=makeQuery(id+"F0.imprint","IMPRINT",FACE,{"disambiguationData":[TD([[makeQuery(id+"F0.imprint","IMPRINT",EDGE,{"derivedFrom":subQ5}),1.0]])]});}
            var Q1;
            {var subQ0=sQuery(id+"F0.wireOp",EDGE,"E14");var subQ1=sQuery(id+"F0.wireOp",EDGE,"E11.bottom");var subQ2=makeQuery(id+"F0.imprint","INTERSECT",VERTEX,{"derivedFrom":[subQ1,subQ0]});Q1=makeQuery(id+"F0.imprint","IMPRINT",FACE,{"disambiguationData":[TD([[makeQuery(id+"F0.imprint","IMPRINT",EDGE,{"disambiguationData":[TD([[subQ2,-1.0]])],"derivedFrom":subQ1}),-1.0]])]});}
            var Q2;
            {var subQ0=sQuery(id+"F0.wireOp",EDGE,"E11.right");Q2=makeQuery(id+"F0.imprint","IMPRINT",FACE,{"disambiguationData":[TD([[makeQuery(id+"F0.imprint","IMPRINT",EDGE,{"derivedFrom":subQ0}),-1.0]])]});}
            var Q3;
            {var subQ0=sQuery(id+"F0.wireOp",EDGE,"E15");var subQ1=sQuery(id+"F0.wireOp",EDGE,"E11.top");var subQ2=makeQuery(id+"F0.imprint","INTERSECT",VERTEX,{"derivedFrom":[subQ1,subQ0]});Q3=makeQuery(id+"F0.imprint","IMPRINT",FACE,{"disambiguationData":[TD([[makeQuery(id+"F0.imprint","IMPRINT",EDGE,{"disambiguationData":[TD([[subQ2,-1.0]])],"derivedFrom":subQ1}),1.0]])]});}
            var Q4;
            {var subQ0=sQuery(id+"F0.wireOp",EDGE,"E39");var subQ1=sQuery(id+"F0.wireOp",EDGE,"E15");var subQ2=makeQuery(id+"F0.imprint","INTERSECT",VERTEX,{"disambiguationData":[OD(1.0)],"derivedFrom":[subQ1,subQ0]});Q4=makeQuery(id+"F0.imprint","IMPRINT",FACE,{"disambiguationData":[TD([[makeQuery(id+"F0.imprint","IMPRINT",EDGE,{"disambiguationData":[TD([[subQ2,-1.0]])],"derivedFrom":subQ1}),-1.0]])]});}
            var Q5;
            {var subQ0=sQuery(id+"F0.wireOp",EDGE,"E39");var subQ1=sQuery(id+"F0.wireOp",EDGE,"E15");var subQ2=makeQuery(id+"F0.imprint","INTERSECT",VERTEX,{"disambiguationData":[OD(1.0)],"derivedFrom":[subQ1,subQ0]});Q5=makeQuery(id+"F0.imprint","IMPRINT",FACE,{"disambiguationData":[TD([[makeQuery(id+"F0.imprint","IMPRINT",EDGE,{"disambiguationData":[TD([[subQ2,-1.0]])],"derivedFrom":subQ1}),1.0]])]});}
            var Q6;
            {var subQ0=sQuery(id+"F0.wireOp",EDGE,"E38");var subQ1=sQuery(id+"F0.wireOp",EDGE,"E15");var subQ2=makeQuery(id+"F0.imprint","INTERSECT",VERTEX,{"disambiguationData":[OD(0.0)],"derivedFrom":[subQ1,subQ0]});Q6=makeQuery(id+"F0.imprint","IMPRINT",FACE,{"disambiguationData":[TD([[makeQuery(id+"F0.imprint","IMPRINT",EDGE,{"disambiguationData":[TD([[subQ2,-1.0]])],"derivedFrom":subQ1}),1.0]])]});}
            var Q7;
            {var subQ0=sQuery(id+"F0.wireOp",EDGE,"E38");var subQ1=sQuery(id+"F0.wireOp",EDGE,"E15");var subQ2=makeQuery(id+"F0.imprint","INTERSECT",VERTEX,{"disambiguationData":[OD(0.0)],"derivedFrom":[subQ1,subQ0]});Q7=makeQuery(id+"F0.imprint","IMPRINT",FACE,{"disambiguationData":[TD([[makeQuery(id+"F0.imprint","IMPRINT",EDGE,{"disambiguationData":[TD([[subQ2,-1.0]])],"derivedFrom":subQ1}),-1.0]])]});}
            var Q8;
            {var subQ0=sQuery(id+"F0.wireOp",EDGE,"E37");var subQ1=sQuery(id+"F0.wireOp",EDGE,"E14");var subQ2=makeQuery(id+"F0.imprint","INTERSECT",VERTEX,{"disambiguationData":[OD(1.0)],"derivedFrom":[subQ1,subQ0]});Q8=makeQuery(id+"F0.imprint","IMPRINT",FACE,{"disambiguationData":[TD([[makeQuery(id+"F0.imprint","IMPRINT",EDGE,{"disambiguationData":[TD([[subQ2,-1.0]])],"derivedFrom":subQ1}),-1.0]])]});}
            var Q9;
            {var subQ0=sQuery(id+"F0.wireOp",EDGE,"E37");var subQ1=sQuery(id+"F0.wireOp",EDGE,"E14");var subQ2=makeQuery(id+"F0.imprint","INTERSECT",VERTEX,{"disambiguationData":[OD(1.0)],"derivedFrom":[subQ1,subQ0]});Q9=makeQuery(id+"F0.imprint","IMPRINT",FACE,{"disambiguationData":[TD([[makeQuery(id+"F0.imprint","IMPRINT",EDGE,{"disambiguationData":[TD([[subQ2,-1.0]])],"derivedFrom":subQ1}),1.0]])]});}
            var Q10;
            {var subQ0=sQuery(id+"F0.wireOp",EDGE,"E36");var subQ1=sQuery(id+"F0.wireOp",EDGE,"E14");var subQ2=makeQuery(id+"F0.imprint","INTERSECT",VERTEX,{"disambiguationData":[OD(0.0)],"derivedFrom":[subQ1,subQ0]});Q10=makeQuery(id+"F0.imprint","IMPRINT",FACE,{"disambiguationData":[TD([[makeQuery(id+"F0.imprint","IMPRINT",EDGE,{"disambiguationData":[TD([[subQ2,-1.0]])],"derivedFrom":subQ1}),1.0]])]});}
            var Q11;
            {var subQ0=sQuery(id+"F0.wireOp",EDGE,"E36");var subQ1=sQuery(id+"F0.wireOp",EDGE,"E14");var subQ2=makeQuery(id+"F0.imprint","INTERSECT",VERTEX,{"disambiguationData":[OD(0.0)],"derivedFrom":[subQ1,subQ0]});Q11=makeQuery(id+"F0.imprint","IMPRINT",FACE,{"disambiguationData":[TD([[makeQuery(id+"F0.imprint","IMPRINT",EDGE,{"disambiguationData":[TD([[subQ2,-1.0]])],"derivedFrom":subQ1}),-1.0]])]});}
            var Q12;
            {var subQ0=sQuery(id+"F0.wireOp",EDGE,"E32");var subQ1=sQuery(id+"F0.wireOp",EDGE,"E15");var subQ2=makeQuery(id+"F0.imprint","INTERSECT",VERTEX,{"disambiguationData":[OD(0.0)],"derivedFrom":[subQ1,subQ0]});Q12=makeQuery(id+"F0.imprint","IMPRINT",FACE,{"disambiguationData":[TD([[makeQuery(id+"F0.imprint","IMPRINT",EDGE,{"disambiguationData":[TD([[subQ2,-1.0]])],"derivedFrom":subQ1}),1.0]])]});}
            var Q13;
            {var subQ0=sQuery(id+"F0.wireOp",EDGE,"E32");var subQ1=sQuery(id+"F0.wireOp",EDGE,"E15");var subQ2=makeQuery(id+"F0.imprint","INTERSECT",VERTEX,{"disambiguationData":[OD(0.0)],"derivedFrom":[subQ1,subQ0]});Q13=makeQuery(id+"F0.imprint","IMPRINT",FACE,{"disambiguationData":[TD([[makeQuery(id+"F0.imprint","IMPRINT",EDGE,{"disambiguationData":[TD([[subQ2,-1.0]])],"derivedFrom":subQ1}),-1.0]])]});}
            var Q14;
            {var subQ0=sQuery(id+"F0.wireOp",EDGE,"E33");var subQ1=sQuery(id+"F0.wireOp",EDGE,"E15");var subQ2=makeQuery(id+"F0.imprint","INTERSECT",VERTEX,{"disambiguationData":[OD(0.0)],"derivedFrom":[subQ1,subQ0]});Q14=makeQuery(id+"F0.imprint","IMPRINT",FACE,{"disambiguationData":[TD([[makeQuery(id+"F0.imprint","IMPRINT",EDGE,{"disambiguationData":[TD([[subQ2,-1.0]])],"derivedFrom":subQ1}),-1.0]])]});}
            var Q15;
            {var subQ0=sQuery(id+"F0.wireOp",EDGE,"E33");var subQ1=sQuery(id+"F0.wireOp",EDGE,"E15");var subQ2=makeQuery(id+"F0.imprint","INTERSECT",VERTEX,{"disambiguationData":[OD(0.0)],"derivedFrom":[subQ1,subQ0]});Q15=makeQuery(id+"F0.imprint","IMPRINT",FACE,{"disambiguationData":[TD([[makeQuery(id+"F0.imprint","IMPRINT",EDGE,{"disambiguationData":[TD([[subQ2,-1.0]])],"derivedFrom":subQ1}),1.0]])]});}
            var Q16;
            {var subQ0=sQuery(id+"F0.wireOp",EDGE,"E28");var subQ1=sQuery(id+"F0.wireOp",EDGE,"E14");var subQ2=makeQuery(id+"F0.imprint","INTERSECT",VERTEX,{"disambiguationData":[OD(0.0)],"derivedFrom":[subQ1,subQ0]});Q16=makeQuery(id+"F0.imprint","IMPRINT",FACE,{"disambiguationData":[TD([[makeQuery(id+"F0.imprint","IMPRINT",EDGE,{"disambiguationData":[TD([[subQ2,-1.0]])],"derivedFrom":subQ1}),1.0]])]});}
            var Q17;
            {var subQ0=sQuery(id+"F0.wireOp",EDGE,"E28");var subQ1=sQuery(id+"F0.wireOp",EDGE,"E14");var subQ2=makeQuery(id+"F0.imprint","INTERSECT",VERTEX,{"disambiguationData":[OD(0.0)],"derivedFrom":[subQ1,subQ0]});Q17=makeQuery(id+"F0.imprint","IMPRINT",FACE,{"disambiguationData":[TD([[makeQuery(id+"F0.imprint","IMPRINT",EDGE,{"disambiguationData":[TD([[subQ2,-1.0]])],"derivedFrom":subQ1}),-1.0]])]});}
            var Q18;
            {var subQ0=sQuery(id+"F0.wireOp",EDGE,"E29");var subQ1=sQuery(id+"F0.wireOp",EDGE,"E14");var subQ2=makeQuery(id+"F0.imprint","INTERSECT",VERTEX,{"disambiguationData":[OD(0.0)],"derivedFrom":[subQ1,subQ0]});Q18=makeQuery(id+"F0.imprint","IMPRINT",FACE,{"disambiguationData":[TD([[makeQuery(id+"F0.imprint","IMPRINT",EDGE,{"disambiguationData":[TD([[subQ2,-1.0]])],"derivedFrom":subQ1}),-1.0]])]});}
            var Q19;
            {var subQ0=sQuery(id+"F0.wireOp",EDGE,"E29");var subQ1=sQuery(id+"F0.wireOp",EDGE,"E14");var subQ2=makeQuery(id+"F0.imprint","INTERSECT",VERTEX,{"disambiguationData":[OD(0.0)],"derivedFrom":[subQ1,subQ0]});Q19=makeQuery(id+"F0.imprint","IMPRINT",FACE,{"disambiguationData":[TD([[makeQuery(id+"F0.imprint","IMPRINT",EDGE,{"disambiguationData":[TD([[subQ2,-1.0]])],"derivedFrom":subQ1}),1.0]])]});}
            extrude(context, id + "F3", {"entities" : qUnion([Q0, Q1, Q2, Q3, Q4, Q5, Q6, Q7, Q8, Q9, Q10, Q11, Q12, Q13, Q14, Q15, Q16, Q17, Q18, Q19]), "operationType" : NewBodyOperationType.REMOVE, "oppositeDirection" : true, "depth" : 25 * mm});
        }
        {
            var Q0;
            {var subQ2=sQuery(id+"F0.wireOp",EDGE,"E0.bottom");var subQ4=sQuery(id+"F0.wireOp",EDGE,"E3");var subQ8=makeQuery(id+"F0.imprint","INTERSECT",VERTEX,{"derivedFrom":[subQ2,subQ4]});Q0=makeQuery(id+"F0.imprint","IMPRINT",FACE,{"disambiguationData":[TD([[makeQuery(id+"F0.imprint","IMPRINT",EDGE,{"disambiguationData":[TD([[subQ8,-1.0]])],"derivedFrom":subQ2}),1.0]])]});}
            var Q1;
            {var subQ3=sQuery(id+"F0.wireOp",EDGE,"E24");var subQ5=sQuery(id+"F0.wireOp",EDGE,"E0.bottom");var subQ6=makeQuery(id+"F0.imprint","INTERSECT",VERTEX,{"derivedFrom":[subQ5,subQ3]});Q1=makeQuery(id+"F0.imprint","IMPRINT",FACE,{"disambiguationData":[TD([[makeQuery(id+"F0.imprint","IMPRINT",EDGE,{"disambiguationData":[TD([[subQ6,-1.0]])],"derivedFrom":subQ5}),-1.0]])]});}
            var Q2;
            {var subQ0=sQuery(id+"F0.wireOp",EDGE,"E24");var subQ1=sQuery(id+"F0.wireOp",EDGE,"E0.bottom");var subQ2=makeQuery(id+"F0.imprint","INTERSECT",VERTEX,{"derivedFrom":[subQ1,subQ0]});Q2=makeQuery(id+"F0.imprint","IMPRINT",FACE,{"disambiguationData":[TD([[makeQuery(id+"F0.imprint","IMPRINT",EDGE,{"disambiguationData":[TD([[subQ2,-1.0]])],"derivedFrom":subQ1}),1.0]])]});}
            var Q3;
            {var subQ5=sQuery(id+"F0.wireOp",EDGE,"E14");var subQ7=sQuery(id+"F0.wireOp",EDGE,"E7");var subQ8=makeQuery(id+"F0.imprint","INTERSECT",VERTEX,{"derivedFrom":[subQ7,subQ5]});Q3=makeQuery(id+"F0.imprint","IMPRINT",FACE,{"disambiguationData":[TD([[makeQuery(id+"F0.imprint","IMPRINT",EDGE,{"disambiguationData":[TD([[subQ8,-1.0]])],"derivedFrom":subQ7}),-1.0]])]});}
            var Q4;
            {var subQ0=sQuery(id+"F0.wireOp",EDGE,"E28");var subQ1=sQuery(id+"F0.wireOp",EDGE,"E14");var subQ2=makeQuery(id+"F0.imprint","INTERSECT",VERTEX,{"disambiguationData":[OD(1.0)],"derivedFrom":[subQ1,subQ0]});Q4=makeQuery(id+"F0.imprint","IMPRINT",FACE,{"disambiguationData":[TD([[makeQuery(id+"F0.imprint","IMPRINT",EDGE,{"disambiguationData":[TD([[subQ2,-1.0]])],"derivedFrom":subQ1}),1.0]])]});}
            var Q5;
            {var subQ0=sQuery(id+"F0.wireOp",EDGE,"E28");var subQ1=sQuery(id+"F0.wireOp",EDGE,"E14");var subQ2=makeQuery(id+"F0.imprint","INTERSECT",VERTEX,{"disambiguationData":[OD(1.0)],"derivedFrom":[subQ1,subQ0]});Q5=makeQuery(id+"F0.imprint","IMPRINT",FACE,{"disambiguationData":[TD([[makeQuery(id+"F0.imprint","IMPRINT",EDGE,{"disambiguationData":[TD([[subQ2,-1.0]])],"derivedFrom":subQ1}),-1.0]])]});}
            var Q6;
            {var subQ0=sQuery(id+"F0.wireOp",EDGE,"E31");var subQ6=sQuery(id+"F0.wireOp",EDGE,"E7");var subQ9=makeQuery(id+"F0.imprint","INTERSECT",VERTEX,{"derivedFrom":[subQ6,subQ0]});Q6=makeQuery(id+"F0.imprint","IMPRINT",FACE,{"disambiguationData":[TD([[makeQuery(id+"F0.imprint","IMPRINT",EDGE,{"disambiguationData":[TD([[subQ9,-1.0]])],"derivedFrom":subQ6}),-1.0]])]});}
            var Q7;
            {var subQ3=sQuery(id+"F0.wireOp",EDGE,"E24");var subQ5=sQuery(id+"F0.wireOp",EDGE,"E0.left");var subQ6=makeQuery(id+"F0.imprint","INTERSECT",VERTEX,{"derivedFrom":[subQ5,subQ3]});Q7=makeQuery(id+"F0.imprint","IMPRINT",FACE,{"disambiguationData":[TD([[makeQuery(id+"F0.imprint","IMPRINT",EDGE,{"disambiguationData":[TD([[subQ6,-1.0]])],"derivedFrom":subQ5}),1.0]])]});}
            var Q8;
            {var subQ0=sQuery(id+"F0.wireOp",EDGE,"E24");var subQ1=sQuery(id+"F0.wireOp",EDGE,"E0.left");var subQ2=makeQuery(id+"F0.imprint","INTERSECT",VERTEX,{"derivedFrom":[subQ1,subQ0]});Q8=makeQuery(id+"F0.imprint","IMPRINT",FACE,{"disambiguationData":[TD([[makeQuery(id+"F0.imprint","IMPRINT",EDGE,{"disambiguationData":[TD([[subQ2,-1.0]])],"derivedFrom":subQ1}),-1.0]])]});}
            var Q9;
            {var subQ0=sQuery(id+"F0.wireOp",EDGE,"E3");var subQ1=sQuery(id+"F0.wireOp",EDGE,"E0.left");var subQ2=makeQuery(id+"F0.imprint","INTERSECT",VERTEX,{"derivedFrom":[subQ1,subQ0]});Q9=makeQuery(id+"F0.imprint","IMPRINT",FACE,{"disambiguationData":[TD([[makeQuery(id+"F0.imprint","IMPRINT",EDGE,{"disambiguationData":[TD([[subQ2,-1.0]])],"derivedFrom":subQ1}),1.0]])]});}
            var Q10;
            {var subQ0=sQuery(id+"F0.wireOp",EDGE,"E3");var subQ1=sQuery(id+"F0.wireOp",EDGE,"E0.bottom");var subQ2=makeQuery(id+"F0.imprint","INTERSECT",VERTEX,{"derivedFrom":[subQ1,subQ0]});Q10=makeQuery(id+"F0.imprint","IMPRINT",FACE,{"disambiguationData":[TD([[makeQuery(id+"F0.imprint","IMPRINT",EDGE,{"disambiguationData":[TD([[subQ2,-1.0]])],"derivedFrom":subQ1}),-1.0]])]});}
            extrude(context, id + "F4", {"entities" : qUnion([Q0, Q1, Q2, Q3, Q4, Q5, Q6, Q7, Q8, Q9, Q10]), "operationType" : NewBodyOperationType.REMOVE, "oppositeDirection" : true, "depth" : 2.5 * mm});
        }
        {
            var Q0;
            {var subQ0=sQuery(id+"F0.wireOp",EDGE,"E25");var subQ1=sQuery(id+"F0.wireOp",EDGE,"E0.bottom");var subQ2=makeQuery(id+"F0.imprint","INTERSECT",VERTEX,{"derivedFrom":[subQ1,subQ0]});Q0=makeQuery(id+"F0.imprint","IMPRINT",FACE,{"disambiguationData":[TD([[makeQuery(id+"F0.imprint","IMPRINT",EDGE,{"disambiguationData":[TD([[subQ2,-1.0]])],"derivedFrom":subQ1}),-1.0]])]});}
            var Q1;
            {var subQ0=sQuery(id+"F0.wireOp",EDGE,"E6");var subQ1=sQuery(id+"F0.wireOp",EDGE,"E0.right");var subQ2=makeQuery(id+"F0.imprint","INTERSECT",VERTEX,{"derivedFrom":[subQ1,subQ0]});Q1=makeQuery(id+"F0.imprint","IMPRINT",FACE,{"disambiguationData":[TD([[makeQuery(id+"F0.imprint","IMPRINT",EDGE,{"disambiguationData":[TD([[subQ2,-1.0]])],"derivedFrom":subQ1}),-1.0]])]});}
            var Q2;
            {var subQ3=sQuery(id+"F0.wireOp",EDGE,"E25");var subQ6=sQuery(id+"F0.wireOp",EDGE,"E0.bottom");var subQ7=makeQuery(id+"F0.imprint","INTERSECT",VERTEX,{"derivedFrom":[subQ6,subQ3]});Q2=makeQuery(id+"F0.imprint","IMPRINT",FACE,{"disambiguationData":[TD([[makeQuery(id+"F0.imprint","IMPRINT",EDGE,{"disambiguationData":[TD([[subQ7,-1.0]])],"derivedFrom":subQ6}),1.0]])]});}
            var Q3;
            {var subQ0=sQuery(id+"F0.wireOp",EDGE,"E34");var subQ1=sQuery(id+"F0.wireOp",EDGE,"E0.bottom");var subQ2=makeQuery(id+"F0.imprint","INTERSECT",VERTEX,{"derivedFrom":[subQ1,subQ0]});Q3=makeQuery(id+"F0.imprint","IMPRINT",FACE,{"disambiguationData":[TD([[makeQuery(id+"F0.imprint","IMPRINT",EDGE,{"disambiguationData":[TD([[subQ2,-1.0]])],"derivedFrom":subQ1}),1.0]])]});}
            var Q4;
            {var subQ0=sQuery(id+"F0.wireOp",EDGE,"E25");var subQ1=sQuery(id+"F0.wireOp",EDGE,"E0.right");var subQ2=makeQuery(id+"F0.imprint","INTERSECT",VERTEX,{"derivedFrom":[subQ1,subQ0]});Q4=makeQuery(id+"F0.imprint","IMPRINT",FACE,{"disambiguationData":[TD([[makeQuery(id+"F0.imprint","IMPRINT",EDGE,{"disambiguationData":[TD([[subQ2,-1.0]])],"derivedFrom":subQ1}),1.0]])]});}
            var Q5;
            {var subQ3=sQuery(id+"F0.wireOp",EDGE,"E25");var subQ7=sQuery(id+"F0.wireOp",EDGE,"E0.right");var subQ8=makeQuery(id+"F0.imprint","INTERSECT",VERTEX,{"derivedFrom":[subQ7,subQ3]});Q5=makeQuery(id+"F0.imprint","IMPRINT",FACE,{"disambiguationData":[TD([[makeQuery(id+"F0.imprint","IMPRINT",EDGE,{"disambiguationData":[TD([[subQ8,-1.0]])],"derivedFrom":subQ7}),-1.0]])]});}
            var Q6;
            {var subQ1=sQuery(id+"F0.wireOp",EDGE,"E0.bottom");var subQ7=sQuery(id+"F0.wireOp",EDGE,"E34");var subQ9=makeQuery(id+"F0.imprint","INTERSECT",VERTEX,{"derivedFrom":[subQ1,subQ7]});Q6=makeQuery(id+"F0.imprint","IMPRINT",FACE,{"disambiguationData":[TD([[makeQuery(id+"F0.imprint","IMPRINT",EDGE,{"disambiguationData":[TD([[subQ9,-1.0]])],"derivedFrom":subQ1}),-1.0]])]});}
            var Q7;
            {var subQ0=sQuery(id+"F0.wireOp",EDGE,"E34");var subQ6=sQuery(id+"F0.wireOp",EDGE,"E8");var subQ9=makeQuery(id+"F0.imprint","INTERSECT",VERTEX,{"derivedFrom":[subQ6,subQ0]});Q7=makeQuery(id+"F0.imprint","IMPRINT",FACE,{"disambiguationData":[TD([[makeQuery(id+"F0.imprint","IMPRINT",EDGE,{"disambiguationData":[TD([[subQ9,-1.0]])],"derivedFrom":subQ6}),-1.0]])]});}
            var Q8;
            {var subQ5=sQuery(id+"F0.wireOp",EDGE,"E15");var subQ7=sQuery(id+"F0.wireOp",EDGE,"E8");var subQ8=makeQuery(id+"F0.imprint","INTERSECT",VERTEX,{"derivedFrom":[subQ7,subQ5]});Q8=makeQuery(id+"F0.imprint","IMPRINT",FACE,{"disambiguationData":[TD([[makeQuery(id+"F0.imprint","IMPRINT",EDGE,{"disambiguationData":[TD([[subQ8,-1.0]])],"derivedFrom":subQ7}),-1.0]])]});}
            var Q9;
            {var subQ0=sQuery(id+"F0.wireOp",EDGE,"E32");var subQ1=sQuery(id+"F0.wireOp",EDGE,"E15");var subQ2=makeQuery(id+"F0.imprint","INTERSECT",VERTEX,{"disambiguationData":[OD(1.0)],"derivedFrom":[subQ1,subQ0]});Q9=makeQuery(id+"F0.imprint","IMPRINT",FACE,{"disambiguationData":[TD([[makeQuery(id+"F0.imprint","IMPRINT",EDGE,{"disambiguationData":[TD([[subQ2,-1.0]])],"derivedFrom":subQ1}),1.0]])]});}
            var Q10;
            {var subQ0=sQuery(id+"F0.wireOp",EDGE,"E32");var subQ1=sQuery(id+"F0.wireOp",EDGE,"E15");var subQ2=makeQuery(id+"F0.imprint","INTERSECT",VERTEX,{"disambiguationData":[OD(1.0)],"derivedFrom":[subQ1,subQ0]});Q10=makeQuery(id+"F0.imprint","IMPRINT",FACE,{"disambiguationData":[TD([[makeQuery(id+"F0.imprint","IMPRINT",EDGE,{"disambiguationData":[TD([[subQ2,-1.0]])],"derivedFrom":subQ1}),-1.0]])]});}
            extrude(context, id + "F5", {"entities" : qUnion([Q0, Q1, Q2, Q3, Q4, Q5, Q6, Q7, Q8, Q9, Q10]), "operationType" : NewBodyOperationType.REMOVE, "oppositeDirection" : true, "depth" : 2.5 * mm});
        }
        {
            var Q0;
            {var subQ0=sQuery(id+"F0.wireOp",EDGE,"E37");var subQ1=sQuery(id+"F0.wireOp",EDGE,"E14");var subQ2=makeQuery(id+"F0.imprint","INTERSECT",VERTEX,{"disambiguationData":[OD(0.0)],"derivedFrom":[subQ1,subQ0]});Q0=makeQuery(id+"F0.imprint","IMPRINT",FACE,{"disambiguationData":[TD([[makeQuery(id+"F0.imprint","IMPRINT",EDGE,{"disambiguationData":[TD([[subQ2,-1.0]])],"derivedFrom":subQ1}),1.0]])]});}
            var Q1;
            {var subQ0=sQuery(id+"F0.wireOp",EDGE,"E37");var subQ6=sQuery(id+"F0.wireOp",EDGE,"E14");var subQ7=makeQuery(id+"F0.imprint","INTERSECT",VERTEX,{"disambiguationData":[OD(0.0)],"derivedFrom":[subQ6,subQ0]});Q1=makeQuery(id+"F0.imprint","IMPRINT",FACE,{"disambiguationData":[TD([[makeQuery(id+"F0.imprint","IMPRINT",EDGE,{"disambiguationData":[TD([[subQ7,-1.0]])],"derivedFrom":subQ6}),-1.0]])]});}
            var Q2;
            {var subQ5=sQuery(id+"F0.wireOp",EDGE,"E14");var subQ7=sQuery(id+"F0.wireOp",EDGE,"E9");var subQ8=makeQuery(id+"F0.imprint","INTERSECT",VERTEX,{"derivedFrom":[subQ7,subQ5]});Q2=makeQuery(id+"F0.imprint","IMPRINT",FACE,{"disambiguationData":[TD([[makeQuery(id+"F0.imprint","IMPRINT",EDGE,{"disambiguationData":[TD([[subQ8,-1.0]])],"derivedFrom":subQ7}),-1.0]])]});}
            var Q3;
            {var subQ5=sQuery(id+"F0.wireOp",EDGE,"E9");var subQ7=sQuery(id+"F0.wireOp",EDGE,"E40");var subQ9=makeQuery(id+"F0.imprint","INTERSECT",VERTEX,{"derivedFrom":[subQ5,subQ7]});Q3=makeQuery(id+"F0.imprint","IMPRINT",FACE,{"disambiguationData":[TD([[makeQuery(id+"F0.imprint","IMPRINT",EDGE,{"disambiguationData":[TD([[subQ9,-1.0]])],"derivedFrom":subQ5}),-1.0]])]});}
            var Q4;
            {var subQ5=sQuery(id+"F0.wireOp",EDGE,"E40");var subQ7=sQuery(id+"F0.wireOp",EDGE,"E0.right");var subQ9=makeQuery(id+"F0.imprint","INTERSECT",VERTEX,{"derivedFrom":[subQ7,subQ5]});Q4=makeQuery(id+"F0.imprint","IMPRINT",FACE,{"disambiguationData":[TD([[makeQuery(id+"F0.imprint","IMPRINT",EDGE,{"disambiguationData":[TD([[subQ9,-1.0]])],"derivedFrom":subQ7}),-1.0]])]});}
            var Q5;
            {var subQ1=sQuery(id+"F0.wireOp",EDGE,"E0.top");var subQ7=sQuery(id+"F0.wireOp",EDGE,"E41");var subQ8=makeQuery(id+"F0.imprint","INTERSECT",VERTEX,{"derivedFrom":[subQ1,subQ7]});Q5=makeQuery(id+"F0.imprint","IMPRINT",FACE,{"disambiguationData":[TD([[makeQuery(id+"F0.imprint","IMPRINT",EDGE,{"disambiguationData":[TD([[subQ8,-1.0]])],"derivedFrom":subQ1}),1.0]])]});}
            var Q6;
            {var subQ0=sQuery(id+"F0.wireOp",EDGE,"E40");var subQ1=sQuery(id+"F0.wireOp",EDGE,"E0.right");var subQ2=makeQuery(id+"F0.imprint","INTERSECT",VERTEX,{"derivedFrom":[subQ1,subQ0]});Q6=makeQuery(id+"F0.imprint","IMPRINT",FACE,{"disambiguationData":[TD([[makeQuery(id+"F0.imprint","IMPRINT",EDGE,{"disambiguationData":[TD([[subQ2,-1.0]])],"derivedFrom":subQ1}),1.0]])]});}
            var Q7;
            {var subQ0=sQuery(id+"F0.wireOp",EDGE,"E41");var subQ1=sQuery(id+"F0.wireOp",EDGE,"E0.top");var subQ2=makeQuery(id+"F0.imprint","INTERSECT",VERTEX,{"derivedFrom":[subQ1,subQ0]});Q7=makeQuery(id+"F0.imprint","IMPRINT",FACE,{"disambiguationData":[TD([[makeQuery(id+"F0.imprint","IMPRINT",EDGE,{"disambiguationData":[TD([[subQ2,-1.0]])],"derivedFrom":subQ1}),-1.0]])]});}
            extrude(context, id + "F6", {"entities" : qUnion([Q0, Q1, Q2, Q3, Q4, Q5, Q6, Q7]), "operationType" : NewBodyOperationType.REMOVE, "oppositeDirection" : true, "depth" : 2.5 * mm});
        }
        {
            var Q0;
            {var subQ0=sQuery(id+"F0.wireOp",EDGE,"E39");var subQ1=sQuery(id+"F0.wireOp",EDGE,"E15");var subQ2=makeQuery(id+"F0.imprint","INTERSECT",VERTEX,{"disambiguationData":[OD(0.0)],"derivedFrom":[subQ1,subQ0]});Q0=makeQuery(id+"F0.imprint","IMPRINT",FACE,{"disambiguationData":[TD([[makeQuery(id+"F0.imprint","IMPRINT",EDGE,{"disambiguationData":[TD([[subQ2,-1.0]])],"derivedFrom":subQ1}),1.0]])]});}
            var Q1;
            {var subQ0=sQuery(id+"F0.wireOp",EDGE,"E39");var subQ1=sQuery(id+"F0.wireOp",EDGE,"E15");var subQ2=makeQuery(id+"F0.imprint","INTERSECT",VERTEX,{"disambiguationData":[OD(0.0)],"derivedFrom":[subQ1,subQ0]});Q1=makeQuery(id+"F0.imprint","IMPRINT",FACE,{"disambiguationData":[TD([[makeQuery(id+"F0.imprint","IMPRINT",EDGE,{"disambiguationData":[TD([[subQ2,-1.0]])],"derivedFrom":subQ1}),-1.0]])]});}
            var Q2;
            {var subQ5=sQuery(id+"F0.wireOp",EDGE,"E10");var subQ7=sQuery(id+"F0.wireOp",EDGE,"E15");var subQ8=makeQuery(id+"F0.imprint","INTERSECT",VERTEX,{"derivedFrom":[subQ5,subQ7]});Q2=makeQuery(id+"F0.imprint","IMPRINT",FACE,{"disambiguationData":[TD([[makeQuery(id+"F0.imprint","IMPRINT",EDGE,{"disambiguationData":[TD([[subQ8,-1.0]])],"derivedFrom":subQ5}),-1.0]])]});}
            var Q3;
            {var subQ0=sQuery(id+"F0.wireOp",EDGE,"E43");var subQ7=sQuery(id+"F0.wireOp",EDGE,"E10");var subQ9=makeQuery(id+"F0.imprint","INTERSECT",VERTEX,{"derivedFrom":[subQ7,subQ0]});Q3=makeQuery(id+"F0.imprint","IMPRINT",FACE,{"disambiguationData":[TD([[makeQuery(id+"F0.imprint","IMPRINT",EDGE,{"disambiguationData":[TD([[subQ9,-1.0]])],"derivedFrom":subQ7}),-1.0]])]});}
            var Q4;
            {var subQ0=sQuery(id+"F0.wireOp",EDGE,"E26");var subQ1=sQuery(id+"F0.wireOp",EDGE,"E0.top");var subQ2=makeQuery(id+"F0.imprint","INTERSECT",VERTEX,{"derivedFrom":[subQ1,subQ0]});Q4=makeQuery(id+"F0.imprint","IMPRINT",FACE,{"disambiguationData":[TD([[makeQuery(id+"F0.imprint","IMPRINT",EDGE,{"disambiguationData":[TD([[subQ2,-1.0]])],"derivedFrom":subQ1}),1.0]])]});}
            var Q5;
            {var subQ1=sQuery(id+"F0.wireOp",EDGE,"E0.left");var subQ5=sQuery(id+"F0.wireOp",EDGE,"E42");var subQ6=makeQuery(id+"F0.imprint","INTERSECT",VERTEX,{"derivedFrom":[subQ1,subQ5]});Q5=makeQuery(id+"F0.imprint","IMPRINT",FACE,{"disambiguationData":[TD([[makeQuery(id+"F0.imprint","IMPRINT",EDGE,{"disambiguationData":[TD([[subQ6,-1.0]])],"derivedFrom":subQ1}),1.0]])]});}
            var Q6;
            {var subQ0=sQuery(id+"F0.wireOp",EDGE,"E42");var subQ1=sQuery(id+"F0.wireOp",EDGE,"E0.left");var subQ2=makeQuery(id+"F0.imprint","INTERSECT",VERTEX,{"derivedFrom":[subQ1,subQ0]});Q6=makeQuery(id+"F0.imprint","IMPRINT",FACE,{"disambiguationData":[TD([[makeQuery(id+"F0.imprint","IMPRINT",EDGE,{"disambiguationData":[TD([[subQ2,-1.0]])],"derivedFrom":subQ1}),-1.0]])]});}
            var Q7;
            {var subQ4=sQuery(id+"F0.wireOp",EDGE,"E4");var subQ6=sQuery(id+"F0.wireOp",EDGE,"E0.top");var subQ7=makeQuery(id+"F0.imprint","INTERSECT",VERTEX,{"derivedFrom":[subQ6,subQ4]});Q7=makeQuery(id+"F0.imprint","IMPRINT",FACE,{"disambiguationData":[TD([[makeQuery(id+"F0.imprint","IMPRINT",EDGE,{"disambiguationData":[TD([[subQ7,-1.0]])],"derivedFrom":subQ6}),-1.0]])]});}
            var Q8;
            {var subQ0=sQuery(id+"F0.wireOp",EDGE,"E4");var subQ1=sQuery(id+"F0.wireOp",EDGE,"E0.top");var subQ2=makeQuery(id+"F0.imprint","INTERSECT",VERTEX,{"derivedFrom":[subQ1,subQ0]});Q8=makeQuery(id+"F0.imprint","IMPRINT",FACE,{"disambiguationData":[TD([[makeQuery(id+"F0.imprint","IMPRINT",EDGE,{"disambiguationData":[TD([[subQ2,-1.0]])],"derivedFrom":subQ1}),1.0]])]});}
            var Q9;
            {var subQ0=sQuery(id+"F0.wireOp",EDGE,"E26");var subQ1=sQuery(id+"F0.wireOp",EDGE,"E0.left");var subQ2=makeQuery(id+"F0.imprint","INTERSECT",VERTEX,{"derivedFrom":[subQ1,subQ0]});Q9=makeQuery(id+"F0.imprint","IMPRINT",FACE,{"disambiguationData":[TD([[makeQuery(id+"F0.imprint","IMPRINT",EDGE,{"disambiguationData":[TD([[subQ2,-1.0]])],"derivedFrom":subQ1}),1.0]])]});}
            var Q10;
            {var subQ0=sQuery(id+"F0.wireOp",EDGE,"E26");var subQ1=sQuery(id+"F0.wireOp",EDGE,"E0.top");var subQ2=makeQuery(id+"F0.imprint","INTERSECT",VERTEX,{"derivedFrom":[subQ1,subQ0]});Q10=makeQuery(id+"F0.imprint","IMPRINT",FACE,{"disambiguationData":[TD([[makeQuery(id+"F0.imprint","IMPRINT",EDGE,{"disambiguationData":[TD([[subQ2,-1.0]])],"derivedFrom":subQ1}),-1.0]])]});}
            extrude(context, id + "F7", {"entities" : qUnion([Q0, Q1, Q2, Q3, Q4, Q5, Q6, Q7, Q8, Q9, Q10]), "operationType" : NewBodyOperationType.REMOVE, "oppositeDirection" : true, "depth" : 2.5 * mm});
        }
    });
